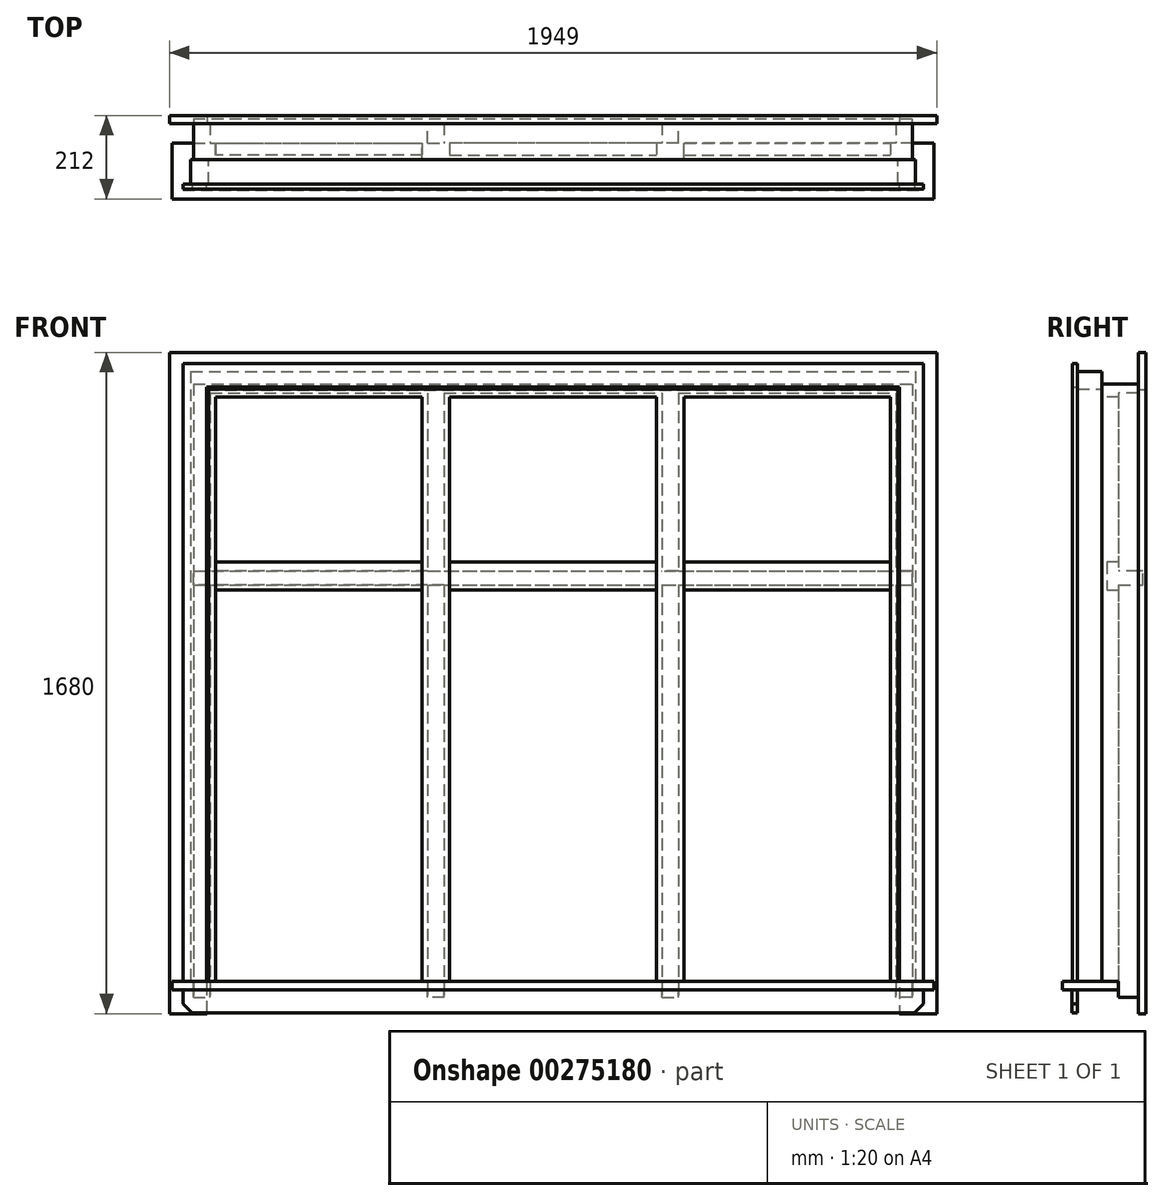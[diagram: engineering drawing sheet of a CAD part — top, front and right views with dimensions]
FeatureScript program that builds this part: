
annotation { "Feature Type Name" : "Feature", "Feature Type Description" : "" }
export const myFeature = defineFeature(function(context is Context, id is Id, definition is map)
    precondition{}
    {
        {
            var Q0;
            Q0=qCreatedBy(makeId("Top.planeOp"),FACE);
            var sketch = newSketch(context, id + "F0", { "sketchPlane" : qUnion([Q0])});
            skLineSegment(sketch, "E0", {"start": v(276.5, 0) * mm, "end": v(262.5, 0) * mm});
            skLineSegment(sketch, "E1", {"start": v(262.5, 0) * mm, "end": v(262.5, -42) * mm});
            skLineSegment(sketch, "E2", {"start": v(262.5, -42) * mm, "end": v(332.5, -42) * mm});
            skLineSegment(sketch, "E3", {"start": v(332.5, -42) * mm, "end": v(332.5, 0) * mm});
            skLineSegment(sketch, "E4", {"start": v(332.5, 0) * mm, "end": v(318.5, 0) * mm});
            skLineSegment(sketch, "E5", {"start": v(318.5, 0) * mm, "end": v(318.5, 50) * mm});
            skLineSegment(sketch, "E6", {"start": v(318.5, 50) * mm, "end": v(276.5, 50) * mm});
            skLineSegment(sketch, "E7", {"start": v(276.5, 50) * mm, "end": v(276.5, 0) * mm});
            skLineSegment(sketch, "E8", {"start": v(857.5, 0) * mm, "end": v(857.5, -42) * mm});
            skLineSegment(sketch, "E9", {"start": v(857.5, -42) * mm, "end": v(913.5, -42) * mm});
            skLineSegment(sketch, "E10", {"start": v(913.5, -42) * mm, "end": v(913.5, 50) * mm});
            skLineSegment(sketch, "E11", {"start": v(913.5, 50) * mm, "end": v(871.5, 50) * mm});
            skLineSegment(sketch, "E12", {"start": v(871.5, 50) * mm, "end": v(871.5, 0) * mm});
            skLineSegment(sketch, "E13", {"start": v(871.5, 0) * mm, "end": v(857.5, 0) * mm});
            skSolve(sketch);
        }
        {
            var Q0;
            Q0=qSketchRegion(id+"F0",true);
            extrude(context, id + "F1", {"entities" : qUnion([Q0]), "depth" : 1485 * mm});
        }
        {
            var Q0;
            Q0=makeQuery(id+"F1.opExtrude","CAP_FACE",FACE,{"disambiguationData":[OSD([sQuery(id+"F0.wireOp",EDGE,"E8"),sQuery(id+"F0.wireOp",EDGE,"E9"),sQuery(id+"F0.wireOp",EDGE,"E10"),sQuery(id+"F0.wireOp",EDGE,"E11"),sQuery(id+"F0.wireOp",EDGE,"E12"),sQuery(id+"F0.wireOp",EDGE,"E13")])],"isStart":false});
            var sketch = newSketch(context, id + "F2", { "sketchPlane" : qUnion([Q0])});
            skLineSegment(sketch, "E14.bottom", {"start": v(913.5, -42) * mm, "end": v(0, -42) * mm});
            skLineSegment(sketch, "E14.top", {"start": v(913.5, 0) * mm, "end": v(0, 0) * mm});
            skLineSegment(sketch, "E14.left", {"start": v(913.5, -42) * mm, "end": v(913.5, 0) * mm});
            skLineSegment(sketch, "E14.right", {"start": v(0, -42) * mm, "end": v(0, 0) * mm});
            skSolve(sketch);
        }
        {
            var Q0;
            Q0=qSketchRegion(id+"F2",true);
            extrude(context, id + "F3", {"entities" : qUnion([Q0]), "operationType" : NewBodyOperationType.ADD, "depth" : 33 * mm});
        }
        {
            var Q0;
            Q0=makeQuery(id+"F1.opExtrude","CAP_FACE",FACE,{"disambiguationData":[OSD([sQuery(id+"F0.wireOp",EDGE,"E0"),sQuery(id+"F0.wireOp",EDGE,"E1"),sQuery(id+"F0.wireOp",EDGE,"E2"),sQuery(id+"F0.wireOp",EDGE,"E3"),sQuery(id+"F0.wireOp",EDGE,"E4"),sQuery(id+"F0.wireOp",EDGE,"E5"),sQuery(id+"F0.wireOp",EDGE,"E6"),sQuery(id+"F0.wireOp",EDGE,"E7")])],"isStart":true});
            var sketch = newSketch(context, id + "F4", { "sketchPlane" : qUnion([Q0])});
            skLineSegment(sketch, "E15.bottom", {"start": v(967.5, 0) * mm, "end": v(0, 0) * mm});
            skLineSegment(sketch, "E15.top", {"start": v(967.5, 142) * mm, "end": v(0, 142) * mm});
            skLineSegment(sketch, "E15.left", {"start": v(967.5, 0) * mm, "end": v(967.5, 142) * mm});
            skLineSegment(sketch, "E15.right", {"start": v(0, 0) * mm, "end": v(0, 142) * mm});
            skSolve(sketch);
        }
        {
            var Q0;
            Q0=qSketchRegion(id+"F4",true);
            extrude(context, id + "F5", {"entities" : qUnion([Q0]), "operationType" : NewBodyOperationType.ADD, "depth" : 22 * mm});
        }
        {
            var Q0;
            Q0=makeQuery(id+"F3.boolean.opBoolean","MERGE",FACE,{"derivedFrom":[makeQuery(id+"F1.opExtrude","SWEPT_FACE",FACE,{"disambiguationData":[OSD([sQuery(id+"F0.wireOp",EDGE,"E10")])]}),makeQuery(id+"F3.opExtrude","SWEPT_FACE",FACE,{"disambiguationData":[OSD([sQuery(id+"F2.wireOp",EDGE,"E14.left")])]})]});
            var sketch = newSketch(context, id + "F6", { "sketchPlane" : qUnion([Q0])});
            skLineSegment(sketch, "E16", {"start": v(-30, 1065) * mm, "end": v(-30, 995) * mm});
            skLineSegment(sketch, "E17", {"start": v(0, 1007) * mm, "end": v(0, 995) * mm});
            skLineSegment(sketch, "E18", {"start": v(0, 1007) * mm, "end": v(62, 1007) * mm});
            skLineSegment(sketch, "E19", {"start": v(62, 1007) * mm, "end": v(62, 1043) * mm});
            skLineSegment(sketch, "E20", {"start": v(62, 1043) * mm, "end": v(0, 1043) * mm});
            skLineSegment(sketch, "E21", {"start": v(0, 1043) * mm, "end": v(0, 1065) * mm});
            skLineSegment(sketch, "E22", {"start": v(0, 1065) * mm, "end": v(-30, 1065) * mm});
            skLineSegment(sketch, "E23", {"start": v(-30, 995) * mm, "end": v(0, 995) * mm});
            skSolve(sketch);
        }
        {
            var Q0;
            Q0=qSketchRegion(id+"F6",true);
            var Q1;
            Q1=makeQuery(id+"F5.opExtrude","SWEPT_FACE",FACE,{"disambiguationData":[OSD([sQuery(id+"F4.wireOp",EDGE,"E15.right")])]});
            extrude(context, id + "F7", {"entities" : qUnion([Q0]), "operationType" : NewBodyOperationType.ADD, "endBound" : BoundingType.UP_TO_SURFACE, "oppositeDirection" : true, "endBoundEntityFace" : qUnion([Q1]), "depth" : 25 * mm});
        }
        {
            var Q0;
            Q0=makeQuery(id+"F3.boolean.opBoolean","MERGE",FACE,{"derivedFrom":[makeQuery(id+"F1.opExtrude","SWEPT_FACE",FACE,{"disambiguationData":[OSD([sQuery(id+"F0.wireOp",EDGE,"E2")])]}),makeQuery(id+"F1.opExtrude","SWEPT_FACE",FACE,{"disambiguationData":[OSD([sQuery(id+"F0.wireOp",EDGE,"E9")])]}),makeQuery(id+"F3.opExtrude","SWEPT_FACE",FACE,{"disambiguationData":[OSD([sQuery(id+"F2.wireOp",EDGE,"E14.bottom")])]})]});
            var sketch = newSketch(context, id + "F8", { "sketchPlane" : qUnion([Q0])});
            skLineSegment(sketch, "E24", {"start": v(875.5, 0) * mm, "end": v(875.5, 1505) * mm});
            skLineSegment(sketch, "E25", {"start": v(875.5, 1505) * mm, "end": v(0, 1505) * mm});
            skPoint(sketch, "E25.endSnap0", {"position": v(0, 1501.5) * mm});
            skLineSegment(sketch, "E26", {"start": v(0, 1505) * mm, "end": v(0, 1550) * mm});
            skLineSegment(sketch, "E27", {"start": v(0, 1550) * mm, "end": v(920.5, 1550) * mm});
            skLineSegment(sketch, "E28", {"start": v(920.5, 1550) * mm, "end": v(920.5, 0) * mm});
            skLineSegment(sketch, "E29", {"start": v(920.5, 0) * mm, "end": v(875.5, 0) * mm});
            skSolve(sketch);
        }
        {
            var Q0;
            Q0=qSketchRegion(id+"F8",true);
            extrude(context, id + "F9", {"entities" : qUnion([Q0]), "operationType" : NewBodyOperationType.ADD, "depth" : 62 * mm});
        }
        {
            var Q0;
            Q0=makeQuery(id+"F9.opExtrude","CAP_FACE",FACE,{"disambiguationData":[OSD([sQuery(id+"F8.wireOp",EDGE,"E24"),sQuery(id+"F8.wireOp",EDGE,"E25"),sQuery(id+"F8.wireOp",EDGE,"E26"),sQuery(id+"F8.wireOp",EDGE,"E27"),sQuery(id+"F8.wireOp",EDGE,"E28"),sQuery(id+"F8.wireOp",EDGE,"E29")])],"isStart":false});
            var sketch = newSketch(context, id + "F10", { "sketchPlane" : qUnion([Q0])});
            skLineSegment(sketch, "E30", {"start": v(880.5, 0) * mm, "end": v(940.5, 0) * mm});
            skPoint(sketch, "E30.endSnap0", {"position": v(898, 0) * mm});
            skLineSegment(sketch, "E31", {"start": v(880.5, 0) * mm, "end": v(880.5, 1510) * mm});
            skLineSegment(sketch, "E32", {"start": v(880.5, 1510) * mm, "end": v(0, 1510) * mm});
            skLineSegment(sketch, "E33", {"start": v(0, 1510) * mm, "end": v(0, 1570) * mm});
            skPoint(sketch, "E33.endSnap0", {"position": v(0, 1527.5) * mm});
            skLineSegment(sketch, "E34", {"start": v(0, 1570) * mm, "end": v(940.5, 1570) * mm});
            skLineSegment(sketch, "E35", {"start": v(940.5, 1570) * mm, "end": v(940.5, 0) * mm});
            skSolve(sketch);
        }
        {
            var Q0;
            Q0=qSketchRegion(id+"F10",true);
            extrude(context, id + "F11", {"entities" : qUnion([Q0]), "operationType" : NewBodyOperationType.ADD, "depth" : 13 * mm});
        }
        {
            var Q0;
            Q0=makeQuery(id+"F5.opExtrude","SWEPT_FACE",FACE,{"disambiguationData":[OSD([sQuery(id+"F4.wireOp",EDGE,"E15.top")])]});
            cPlane(context, id + "F12", {"entities" : qUnion([Q0]), "cplaneType" : CPlaneType.OFFSET, "offset" : 23 * mm, "oppositeDirection" : true, "width" : 150 * mm, "height" : 150 * mm});
        }
        {
            var Q0;
            Q0=qCreatedBy(id+"F12.planeOp",FACE);
            var sketch = newSketch(context, id + "F13", { "sketchPlane" : qUnion([Q0])});
            skLineSegment(sketch, "E36", {"start": v(940.5, -22) * mm, "end": v(940.5, -57) * mm});
            skLineSegment(sketch, "E37", {"start": v(940.5, -57) * mm, "end": v(917.5, -80) * mm});
            skLineSegment(sketch, "E38", {"start": v(917.5, -80) * mm, "end": v(0, -80) * mm});
            skLineSegment(sketch, "E39", {"start": v(0, -80) * mm, "end": v(0, -22) * mm});
            skLineSegment(sketch, "E40", {"start": v(0, -22) * mm, "end": v(940.5, -22) * mm});
            skSolve(sketch);
        }
        {
            var Q0;
            Q0=qSketchRegion(id+"F13",true);
            extrude(context, id + "F14", {"entities" : qUnion([Q0]), "operationType" : NewBodyOperationType.ADD, "oppositeDirection" : true, "depth" : 15 * mm});
        }
        {
            var Q0;
            Q0=makeQuery(id+"F7.boolean.opBoolean","MERGE",FACE,{"derivedFrom":[makeQuery(id+"F5.boolean.opBoolean","MERGE",FACE,{"derivedFrom":[makeQuery(id+"F3.boolean.opBoolean","MERGE",FACE,{"derivedFrom":[makeQuery(id+"F1.opExtrude","SWEPT_FACE",FACE,{"disambiguationData":[OSD([sQuery(id+"F0.wireOp",EDGE,"E0")])]}),makeQuery(id+"F1.opExtrude","SWEPT_FACE",FACE,{"disambiguationData":[OSD([sQuery(id+"F0.wireOp",EDGE,"E4")])]}),makeQuery(id+"F1.opExtrude","SWEPT_FACE",FACE,{"disambiguationData":[OSD([sQuery(id+"F0.wireOp",EDGE,"E13")])]}),makeQuery(id+"F3.opExtrude","SWEPT_FACE",FACE,{"disambiguationData":[OSD([sQuery(id+"F2.wireOp",EDGE,"E14.top")])]})]}),makeQuery(id+"F5.opExtrude","SWEPT_FACE",FACE,{"disambiguationData":[OSD([sQuery(id+"F4.wireOp",EDGE,"E15.bottom")])]})]}),makeQuery(id+"F7.opExtrude","SWEPT_FACE",FACE,{"disambiguationData":[OSD([sQuery(id+"F6.wireOp",EDGE,"E21")])]})]});
            var sketch = newSketch(context, id + "F15", { "sketchPlane" : qUnion([Q0])});
            skLineSegment(sketch, "E41", {"start": v(-913.5, 1485) * mm, "end": v(-913.5, 1518) * mm});
            skLineSegment(sketch, "E42", {"start": v(-913.5, 1518) * mm, "end": v(0, 1518) * mm});
            skLineSegment(sketch, "E43", {"start": v(0, 1518) * mm, "end": v(0, 1495) * mm});
            skLineSegment(sketch, "E44", {"start": v(0, 1495) * mm, "end": v(-276.5, 1495) * mm});
            skLineSegment(sketch, "E45", {"start": v(-276.5, 1495) * mm, "end": v(-276.5, 1485) * mm});
            skLineSegment(sketch, "E46", {"start": v(-276.5, 1485) * mm, "end": v(-318.5, 1485) * mm});
            skLineSegment(sketch, "E47", {"start": v(-318.5, 1485) * mm, "end": v(-318.5, 1495) * mm});
            skLineSegment(sketch, "E48", {"start": v(-318.5, 1495) * mm, "end": v(-871.5, 1495) * mm});
            skLineSegment(sketch, "E49", {"start": v(-871.5, 1495) * mm, "end": v(-871.5, 1485) * mm});
            skLineSegment(sketch, "E50", {"start": v(-871.5, 1485) * mm, "end": v(-913.5, 1485) * mm});
            skSolve(sketch);
        }
        {
            var Q0;
            Q0=qSketchRegion(id+"F15",true);
            var Q1;
            {var subQ1=sQuery(id+"F0.wireOp",EDGE,"E6");Q1=makeQuery(id+"F7.boolean.opBoolean","SPLIT",FACE,{"disambiguationData":[TD([makeQuery(id+"F7.opExtrude","SWEPT_FACE",FACE,{"disambiguationData":[OSD([sQuery(id+"F6.wireOp",EDGE,"E20")])]})])],"derivedFrom":makeQuery(id+"F1.opExtrude","SWEPT_FACE",FACE,{"disambiguationData":[OSD([subQ1])]})});}
            extrude(context, id + "F16", {"entities" : qUnion([Q0]), "operationType" : NewBodyOperationType.ADD, "endBound" : BoundingType.UP_TO_SURFACE, "endBoundEntityFace" : qUnion([Q1]), "depth" : 25 * mm});
        }
        {
            var Q0;
            Q0=makeQuery(id+"F1.opExtrude","CAP_FACE",FACE,{"disambiguationData":[OSD([sQuery(id+"F0.wireOp",EDGE,"E8"),sQuery(id+"F0.wireOp",EDGE,"E9"),sQuery(id+"F0.wireOp",EDGE,"E10"),sQuery(id+"F0.wireOp",EDGE,"E11"),sQuery(id+"F0.wireOp",EDGE,"E12"),sQuery(id+"F0.wireOp",EDGE,"E13")])],"isStart":true});
            var sketch = newSketch(context, id + "F17", { "sketchPlane" : qUnion([Q0])});
            skLineSegment(sketch, "E51", {"start": v(913.5, 0) * mm, "end": v(913.5, -50) * mm});
            skLineSegment(sketch, "E52", {"start": v(913.5, -50) * mm, "end": v(871.5, -50) * mm});
            skLineSegment(sketch, "E53", {"start": v(871.5, -50) * mm, "end": v(871.5, 0) * mm});
            skLineSegment(sketch, "E54", {"start": v(871.5, 0) * mm, "end": v(913.5, 0) * mm});
            skLineSegment(sketch, "E55", {"start": v(276.5, -50) * mm, "end": v(318.5, -50) * mm});
            skLineSegment(sketch, "E56", {"start": v(318.5, -50) * mm, "end": v(318.5, 0) * mm});
            skLineSegment(sketch, "E57", {"start": v(318.5, 0) * mm, "end": v(276.5, 0) * mm});
            skLineSegment(sketch, "E58", {"start": v(276.5, 0) * mm, "end": v(276.5, -50) * mm});
            skSolve(sketch);
        }
        {
            var Q0;
            Q0=makeQuery(id+"F17.imprint","IMPRINT",FACE,{"disambiguationData":[TD([[makeQuery(id+"F17.imprint","IMPRINT",EDGE,{"derivedFrom":sQuery(id+"F17.wireOp",EDGE,"E55")}),1.0]])]});
            var Q1;
            Q1=makeQuery(id+"F17.imprint","IMPRINT",FACE,{"disambiguationData":[TD([[makeQuery(id+"F17.imprint","IMPRINT",EDGE,{"derivedFrom":sQuery(id+"F17.wireOp",EDGE,"E51")}),-1.0]])]});
            extrude(context, id + "F18", {"entities" : qUnion([Q0, Q1]), "operationType" : NewBodyOperationType.ADD, "depth" : 40 * mm});
        }
        {
            var Q0;
            Q0=makeQuery(id+"F1.opExtrude","SWEPT_BODY",BODY,{"disambiguationData":[OSD([sQuery(id+"F0.wireOp",EDGE,"E0"),sQuery(id+"F0.wireOp",EDGE,"E1"),sQuery(id+"F0.wireOp",EDGE,"E2"),sQuery(id+"F0.wireOp",EDGE,"E3"),sQuery(id+"F0.wireOp",EDGE,"E4"),sQuery(id+"F0.wireOp",EDGE,"E5"),sQuery(id+"F0.wireOp",EDGE,"E6"),sQuery(id+"F0.wireOp",EDGE,"E7")])]});
            var Q1;
            Q1=qCreatedBy(makeId("Right.planeOp"),FACE);
            mirror(context, id + "F19", {"operationType" : NewBodyOperationType.ADD, "entities" : qUnion([Q0]), "mirrorPlane" : qUnion([Q1])});
        }
        {
            var Q0;
            {var subQ2=sQuery(id+"F0.wireOp",EDGE,"E11");var subQ3=sQuery(id+"F6.wireOp",EDGE,"E20");var subQ4=makeQuery(id+"F7.opExtrude","SWEPT_FACE",FACE,{"disambiguationData":[OSD([subQ3])]});var subQ6=sQuery(id+"F0.wireOp",EDGE,"E6");var subQ8=makeQuery(id+"F16.boolean.opBoolean","MERGE",FACE,{"derivedFrom":[makeQuery(id+"F7.boolean.opBoolean","SPLIT",FACE,{"disambiguationData":[TD([subQ4])],"derivedFrom":makeQuery(id+"F1.opExtrude","SWEPT_FACE",FACE,{"disambiguationData":[OSD([subQ6])]})}),makeQuery(id+"F7.boolean.opBoolean","SPLIT",FACE,{"disambiguationData":[TD([subQ4])],"derivedFrom":makeQuery(id+"F1.opExtrude","SWEPT_FACE",FACE,{"disambiguationData":[OSD([subQ2])]})}),makeQuery(id+"F16.opExtrude","CAP_FACE",FACE,{"disambiguationData":[OSD([sQuery(id+"F15.wireOp",EDGE,"E41"),sQuery(id+"F15.wireOp",EDGE,"E42"),sQuery(id+"F15.wireOp",EDGE,"E43"),sQuery(id+"F15.wireOp",EDGE,"E44"),sQuery(id+"F15.wireOp",EDGE,"E45"),sQuery(id+"F15.wireOp",EDGE,"E46"),sQuery(id+"F15.wireOp",EDGE,"E47"),sQuery(id+"F15.wireOp",EDGE,"E48"),sQuery(id+"F15.wireOp",EDGE,"E49"),sQuery(id+"F15.wireOp",EDGE,"E50")])],"isStart":false})]});Q0=makeQuery(id+"F19.boolean.opBoolean","MERGE",FACE,{"derivedFrom":[subQ8,makeQuery(id+"F19.opPattern","COPY",FACE,{"derivedFrom":subQ8,"instanceName":"1"})]});}
            var sketch = newSketch(context, id + "F20", { "sketchPlane" : qUnion([Q0])});
            skLineSegment(sketch, "E59", {"start": v(-879.5, 1503) * mm, "end": v(-879.5, -82) * mm});
            skLineSegment(sketch, "E60", {"start": v(-879.5, -82) * mm, "end": v(-974.5, -82) * mm});
            skLineSegment(sketch, "E61", {"start": v(-974.5, -82) * mm, "end": v(-974.5, 1598) * mm});
            skLineSegment(sketch, "E62", {"start": v(-974.5, 1598) * mm, "end": v(974.5, 1598) * mm});
            skLineSegment(sketch, "E63", {"start": v(974.5, 1598) * mm, "end": v(974.5, -82) * mm});
            skLineSegment(sketch, "E64", {"start": v(974.5, -82) * mm, "end": v(879.5, -82) * mm});
            skLineSegment(sketch, "E65", {"start": v(879.5, -82) * mm, "end": v(879.5, 1503) * mm});
            skLineSegment(sketch, "E66", {"start": v(879.5, 1503) * mm, "end": v(-879.5, 1503) * mm});
            skSolve(sketch);
        }
        {
            var Q0;
            Q0=qSketchRegion(id+"F20",true);
            extrude(context, id + "F21", {"entities" : qUnion([Q0]), "depth" : 20 * mm});
        }
    });
